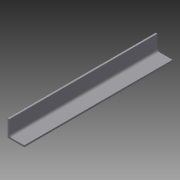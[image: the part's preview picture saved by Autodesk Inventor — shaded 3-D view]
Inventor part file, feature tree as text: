
AUTODESK INVENTOR PART (.ipt)
format: ipt  version: 2014 (Build 180170000, 170)  size: 78,336 bytes
history: native  units: in
note: dims shown in document units (in); Inventor stores cm internally (conversion verified against a paired STEP export)
features: extrude x1, sketch x1
ambient origin geometry x8: Origin, YZ Plane, XZ Plane, XY Plane, X Axis, Y Axis, Z Axis, Center Point
bodies: Solid1 (feature_tree)
feature tree (2):
  extrude  "Extrusion1"  Depth=1.0in
  sketch  "Sketch1"  dims[d0=1.0in d1=1.0in d2=0.1in d3=0.125in d4=8.8583in d5=0.0in]
